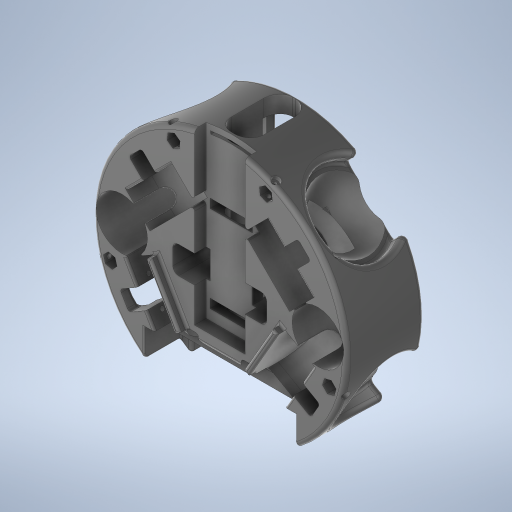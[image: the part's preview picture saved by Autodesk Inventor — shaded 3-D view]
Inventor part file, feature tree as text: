
AUTODESK INVENTOR PART (.ipt)
format: ipt  version: 2023 (Build 270158000, 158)  size: 3,521,024 bytes
history: native  units: mm
features: extrude x76, sketch x76, projected_geometry x35, fillet x19, other x16, chamfer x4, plane x2, mirror x2
ambient origin geometry x8: Origin, YZ Plane, XZ Plane, XY Plane, X Axis, Y Axis, Z Axis, Center Point
bodies: Solid1 (feature_tree)
feature tree (230):
  extrude  "Cilinder"  Depth=54.0mm TaperAngle=0.0deg
  other  "Motor Axis"
  other  "Plano M1"
  other  "Plano M2"
  other  "Plano M3"
  other  "Plano M4"
  extrude  "Roda M1"  Depth=176.0mm
  extrude  "Roda M2"  TaperAngle=60.0deg  [1 undecoded]
  extrude  "Roda M3"  TaperAngle=45.0deg  [1 undecoded]
  extrude  "Roda M4"  TaperAngle=0.0deg  [1 undecoded]
  extrude  "MotorsFitting"  Depth=14.6mm TaperAngle=0.0deg
  fillet  "MotorsCurve"  Radius=55.0mm
  extrude  "Threads M1"  Depth=20.0mm
  extrude  "Threads M2"  Depth=55.0mm
  extrude  "Threads M3"  Depth=20.0mm
  extrude  "Threads M4"  Depth=55.0mm
  extrude  "Threads Head M1"  Depth=20.0mm
  extrude  "Threads Head M2"  Depth=9.4mm
  extrude  "Threads Head M3"  Depth=9.4mm
  extrude  "Threads Head M4"  Depth=23.0mm
  extrude  "Thread Depth M1"  Depth=9.4mm
  extrude  "Thread Depth M2"  Depth=45.0mm
  extrude  "Thread Depth M3"  Depth=45.0mm
  extrude  "Thread Depth M4"  Depth=30.0mm
  extrude  "Threads Nut Head M1"  Depth=32.5mm
  extrude  "Threads Nut Head M2"  Depth=40.0mm TaperAngle=0.0deg
  extrude  "Threads Nut Head M3"  Depth=5.0mm
  extrude  "Threads Nut Head M4"  TaperAngle=0.0deg  [1 undecoded]
  extrude  "Wheel Fitting M1"  Depth=3.0mm
  extrude  "Wheel Fitting M2"  TaperAngle=0.0deg  [1 undecoded]
  extrude  "Wheel Fitting M3"  Depth=30.0mm TaperAngle=360.0deg
  extrude  "Wheel Fitting M4"  Depth=2.0mm
  extrude  "Capacitors"  Depth=6.0mm
  extrude  "Gear Entrance M1"  Depth=19.5mm
  extrude  "Gear Entrance M2"  Depth=10.0mm
  extrude  "Gear Entrance M3"  Depth=2.0mm
  extrude  "Gear Entrance M4"  Depth=3.0mm
  fillet  "Rounding Edges"  Radius=3.0mm
  fillet  "Rounding Motor Entrances"  Radius=6.0mm
  extrude  "Standoff Fitting"  TaperAngle=0.0deg  [1 undecoded]
  extrude  "Standoff Thread M1"  Depth=19.6mm
  extrude  "Standoff Thread M2"  Depth=19.5mm
  extrude  "Standoff Thread M3"  TaperAngle=0.0deg  [1 undecoded]
  extrude  "Standoff Thread M4"  Depth=30.0mm TaperAngle=360.0deg
  other  "Standoff Plane M1"
  other  "Standoff Plane M2"
  other  "Standoff Plane M3"
  other  "Standoff Plane M4"
  extrude  "Standoff Head M1"  Depth=10.0mm
  extrude  "Standoff Head M2"  Depth=2.0mm
  extrude  "Standoff Head M3"  TaperAngle=0.0deg  [1 undecoded]
  extrude  "Standoff Head M4"  Depth=6.0mm
  extrude  "Dribbler Entrance"  Depth=19.5mm
  extrude  "Battery Fitting"  Depth=3.0mm
  fillet  "Motor to Battery Edges"  Radius=3.0mm
  extrude  "Front Kicker"  Depth=11.0mm
  fillet  "Front Edges"  Radius=30.0mm
  extrude  "Cover Inlet"  Depth=10.0mm TaperAngle=0.0deg
  extrude  "Capacitors Holes"  Depth=2.0mm
  extrude  "Dribbler Motor Space"  Depth=6.0mm
  extrude  "IR Holder"  TaperAngle=0.0deg  [1 undecoded]
  fillet  "Dribbler and Kicker Edges"  Radius=19.5mm
  fillet  "Minor Fixes"  Radius=19.5mm
  chamfer  "Dribbler Chanfer"  Distance=30.0mm Angle=360.0deg
  extrude  "Capacitor Cable Fittng 1"  Depth=10.0mm TaperAngle=0.0deg
  fillet  "Capacitor Cable Rounding"  Radius=5.5mm
  extrude  "Special Nut M1"  Depth=5.5mm
  extrude  "Special Nut M2"  Depth=5.5mm
  extrude  "Special Nut M3"  Depth=5.5mm
  extrude  "Special Nut M4"  Depth=5.5mm
  extrude  "Special Nut Cylinder M1"  Depth=5.5mm
  extrude  "Special Nut Cylinder M2"  Depth=5.5mm
  extrude  "Special Nut Cylinder M3"  Depth=5.5mm
  extrude  "Special Nut Cylinder M4"  Depth=4.0mm
  fillet  "Special Nut Rounding"  Radius=4.0mm
  extrude  "Kicker Plate Fit 1"  Depth=4.0mm
  extrude  "Kicker Front Opening"  Depth=17.75mm TaperAngle=0.0deg
  extrude  "Kicker Base Fit"  Depth=4.0mm
  extrude  "Coil and Plinge Fitting"  Depth=4.0mm
  extrude  "Kicker Pkate Plunge Fit"  Depth=17.75mm TaperAngle=0.0deg
  chamfer  "Plunge Entrance 1"  Distance=17.6mm
  chamfer  "Plunge Entrance 2"  Distance=17.6mm
  fillet  "Fillet11"  Radius=15.5mm
  chamfer  "Coil Edges 1"  Distance=17.6mm
  extrude  "Kicker Plate Threads"  Depth=32.0mm
  extrude  "kicker Plate Nut 1"  Depth=35.7mm
  extrude  "Kicker Plate Nut 2"  Depth=68.0mm
  extrude  "Kicker Plunge Fit"  Depth=10.0mm TaperAngle=0.0deg
  fillet  "Kicker Plunge Round"  Radius=12.5mm
  fillet  "Wheel Round"  Radius=14.0mm
  extrude  "Capacitor Cables"  Depth=10.0mm
  fillet  "Capacitor Cable Round 1"  Radius=12.5mm
  fillet  "Capacitor Cable Round 2"  Radius=10.0mm
  extrude  "MotorProtection"  Depth=10.0mm TaperAngle=0.0deg
  fillet  "Motor Protection Round"  Radius=12.5mm
  extrude  "Extrusion86"  Depth=10.0mm
  extrude  "Extrusion87"  Depth=10.0mm TaperAngle=0.0deg
  fillet  "Fillet17"  Radius=12.5mm
  extrude  "Extrusion88"  Depth=10.0mm
  plane  "Work Plane14"
  extrude  "Extrusion89"  Depth=10.0mm TaperAngle=0.0deg
  extrude  "Extrusion91"  Depth=3.0mm
  mirror  "Mirror3"
  fillet  "Fillet18"  Radius=2.0mm
  extrude  "Extrusion92"  Depth=10.0mm
  fillet  "Fillet19"  Radius=22.0mm
  extrude  "Extrusion93"  Depth=10.0mm
  fillet  "Fillet20"  Radius=4.22mm
  extrude  "Extrusion94"  Depth=10.0mm
  extrude  "Extrusion95"  Depth=10.0mm
  other  "Eixo de trabalho1"
  other  "Eixo de trabalho2"
  other  "Eixo de trabalho3"
  other  "Eixo de trabalho4"
  other  "Plano de trabalho16"
  other  "Revolução1"
  other  "Revolução2"
  mirror  "Espelhamento5"
  sketch  "Sketch1"  dims[d0=176.0mm d1=54.0mm d2=0.0mm]
  sketch  "Sketch3"  dims[d3=180.0mm d4=176.0mm]
  sketch  "Sketch4"  dims[d5=60.0deg d6=60.0deg]
  sketch  "Sketch5"  dims[d8=45.0deg d9=45.0deg]
  sketch  "Sketch6"  dims[d10=55.0mm d11=0.0mm]
  sketch  "Sketch7"  dims[d12=20.0mm d13=14.6mm d14=0.0mm d15=55.0mm]
  sketch  "Sketch8"  dims[d16=0.0mm d17=20.0mm]
  sketch  "Sketch9"  dims[d18=14.6mm d19=0.0mm d20=55.0mm]
  sketch  "Sketch10"  dims[d21=0.0mm d22=20.0mm]
  sketch  "Sketch11"  dims[d23=14.6mm d24=0.0mm d25=55.0mm]
  sketch  "Sketch12"  dims[d26=0.0mm d27=20.0mm]
  sketch  "Sketch13"  dims[d28=14.6mm d29=0.0mm d30=9.4mm]
  sketch  "Sketch14"  dims[d32=9.4mm d33=9.4mm]
  sketch  "Sketch15"  dims[d34=23.0mm d35=23.0mm]
  sketch  "Sketch16"  dims[d37=23.0mm d38=9.4mm]
  sketch  "Sketch17"  dims[d39=23.0mm d40=45.0mm]
  sketch  "Sketch18"  dims[d41=45.0mm d42=45.0mm]
  sketch  "Sketch19"  dims[d43=45.0mm d44=30.0mm]
  sketch  "Sketch20"  dims[d45=30.0mm d46=32.5mm]
  sketch  "Sketch21"  dims[d47=32.5mm d48=40.0mm d49=0.0mm]
  sketch  "Sketch22"  dims[d50=22.5mm d51=5.0mm]
  sketch  "Sketch23"  dims[d52=12.5mm d53=0.0mm]
  sketch  "Sketch24"  dims[d54=19.5mm d55=3.0mm]
  sketch  "Sketch25"  dims[d56=19.6mm d58=0.0mm]
  sketch  "Sketch26"  dims[d59=11.0mm d60=30.0mm d62=360.0deg]
  sketch  "Sketch27"  dims[d64=2.0mm d65=2.0mm]
  sketch  "Sketch28"  dims[d66=6.0mm d67=6.0mm]
  sketch  "Sketch29"  dims[d68=19.5mm d69=19.5mm]
  sketch  "Sketch30"  dims[d70=10.0mm d71=0.0mm d72=2.5mm]
  projected_geometry  "Projected Loop1"
  sketch  "Sketch31"  dims[d73=5.0mm d74=2.0mm]
  projected_geometry  "Projected Loop2"
  sketch  "Sketch32"  dims[d75=2.0mm d76=12.5mm d77=3.0mm d78=6.0mm]
  projected_geometry  "Projected Loop3"
  sketch  "Sketch33"  dims[d79=6.0mm d80=0.0mm]
  projected_geometry  "Projected Loop4"
  sketch  "Sketch34"  dims[d81=19.5mm d82=19.6mm]
  sketch  "Sketch35"  dims[d83=19.5mm d84=19.5mm]
  projected_geometry  "Projected Loop5"
  sketch  "Sketch36"  dims[d85=5.0mm d86=0.0mm]
  projected_geometry  "Projected Loop6"
  sketch  "Sketch37"  dims[d87=11.0mm d88=30.0mm d90=360.0deg]
  projected_geometry  "Projected Loop7"
  sketch  "Sketch38"  dims[d92=10.0mm d93=0.0mm d94=5.0mm]
  projected_geometry  "Projected Loop8"
  sketch  "Sketch39"  dims[d95=12.5mm d96=2.0mm]
  sketch  "Sketch40"  dims[d97=2.0mm d98=0.0mm]
  sketch  "Sketch41"  dims[d99=19.5mm d100=6.0mm]
  sketch  "Sketch42"  dims[d101=6.0mm d102=19.5mm]
  sketch  "Sketch43"  dims[d103=19.5mm d104=19.6mm d105=3.0mm]
  sketch  "Sketch44"  dims[d106=0.0mm d107=11.0mm d108=30.0mm d110=360.0deg]
  projected_geometry  "Projected Loop9"
  projected_geometry  "Projected Loop10"
  sketch  "Sketch45"  dims[d112=5.0mm d113=10.0mm d114=0.0mm]
  sketch  "Sketch46"  dims[d115=5.0mm d116=2.0mm]
  projected_geometry  "Projected Loop11"
  projected_geometry  "Projected Loop12"
  sketch  "Sketch48"  dims[d117=2.0mm d118=6.0mm]
  projected_geometry  "Projected Loop14"
  sketch  "Sketch50"  dims[d119=6.0mm d120=0.0mm d121=19.5mm d122=19.5mm]
  projected_geometry  "Projected Loop15"
  sketch  "Sketch59"  dims[d123=19.5mm]
  sketch  "Sketch64"  dims[d124=12.5mm]
  sketch  "Sketch65"  dims[d125=19.6mm]
  projected_geometry  "Projected Loop27"
  sketch  "Sketch66"  dims[d126=3.0mm]
  projected_geometry  "Projected Loop28"
  sketch  "Sketch67"  dims[d127=0.0mm]
  sketch  "Sketch68"  dims[d128=11.0mm d129=30.0mm d131=360.0deg]
  sketch  "Sketch69"  dims[d133=2.5mm d134=10.0mm d135=0.0mm d136=5.5mm]
  sketch  "Sketch70"  dims[d137=5.5mm d138=5.5mm]
  sketch  "Sketch71"  dims[d139=18.0mm d140=0.0mm d141=5.5mm]
  sketch  "Sketch72"  dims[d142=5.5mm d143=5.5mm]
  projected_geometry  "Projected Loop29"
  sketch  "Sketch73"  dims[d144=18.0mm d145=0.0mm d146=5.5mm]
  sketch  "Sketch74"  dims[d147=5.5mm d148=5.5mm]
  projected_geometry  "Projected Loop30"
  sketch  "Sketch75"  dims[d149=18.0mm d150=0.0mm d151=5.5mm]
  projected_geometry  "Projected Loop31"
  sketch  "Sketch76"  dims[d152=5.5mm d153=5.5mm]
  projected_geometry  "Projected Loop32"
  projected_geometry  "Projected Loop33"
  sketch  "Sketch77"  dims[d154=18.0mm d155=0.0mm d156=4.0mm d157=4.0mm]
  projected_geometry  "Projected Loop34"
  projected_geometry  "Projected Loop35"
  projected_geometry  "Projected Loop36"
  projected_geometry  "Projected Loop37"
  sketch  "Sketch78"  dims[d158=17.75mm d159=0.0mm d160=4.0mm]
  sketch  "Sketch80"  dims[d161=4.0mm d162=17.75mm d163=0.0mm]
  projected_geometry  "Projected Loop38"
  projected_geometry  "Projected Loop39"
  projected_geometry  "Projected Loop40"
  projected_geometry  "Projected Loop41"
  sketch  "Sketch81"  dims[d164=4.0mm d165=4.0mm]
  sketch  "Sketch82"  dims[d166=17.75mm d167=0.0mm d168=4.0mm]
  sketch  "Sketch89"  dims[d169=4.0mm d170=17.75mm d171=0.0mm]
  sketch  "Sketch90"  dims[d172=15.5mm]
  sketch  "Sketch92"  dims[d173=32.0mm d174=17.6mm d175=0.0mm]
  sketch  "Sketch93"  dims[d176=15.5mm]
  sketch  "Sketch95"  dims[d177=32.0mm d178=17.6mm d179=0.0mm d180=15.5mm]
  plane  "Work Plane15"
  projected_geometry  "Projected Loop46"
  projected_geometry  "Projected Loop47"
  projected_geometry  "Projected Loop48"
  sketch  "Sketch97"  dims[d181=32.0mm d182=17.6mm d183=0.0mm]
  sketch  "Sketch98"  dims[d184=15.5mm d185=32.0mm]
  projected_geometry  "Projected Loop49"
  projected_geometry  "Projected Loop50"
  projected_geometry  "Projected Loop51"
  sketch  "Sketch99"  dims[d186=17.6mm d187=0.0mm d188=35.7mm]
  sketch  "Esboço100"  dims[d189=4.15mm d190=68.0mm]
  sketch  "Esboço101"  dims[d191=68.0mm d192=50.0mm d193=0.0mm d195=12.5mm d196=14.0mm d197=0.0mm d198=10.0mm d199=12.5mm d200=10.0mm d201=14.0mm d202=0.0mm d203=12.5mm d204=10.0mm d205=14.0mm d206=0.0mm d207=12.5mm d208=10.0mm d209=14.0mm d210=0.0mm d211=3.0mm d212=2.0mm d213=2.0mm d214=2.0mm d215=22.0mm d216=76.0mm d217=4.22mm d218=72.0mm d219=32.0mm d220=4.22mm d221=8.0mm d222=0.0mm d223=3.0mm d224=3.5mm d225=2.436418mm d226=24.0mm d227=0.0mm d228=3.0mm d229=3.5mm d230=2.436418mm d231=24.0mm d232=0.0mm d233=3.0mm d234=3.5mm d235=2.436418mm d236=24.0mm d237=0.0mm d238=3.0mm d239=3.5mm d240=2.436418mm d241=24.0mm d242=0.0mm d243=90.0mm d244=40.0mm d245=0.0mm d246=55.0mm d247=10.0mm d248=0.0mm d249=2.0mm d250=0.0mm d251=2.0mm d252=0.0mm d253=2.0mm d254=0.0mm d255=2.0mm d256=0.0mm d257=2.0mm d258=1.5mm d259=35.0mm d260=120.0mm d261=0.0mm d262=28.5mm d263=8.0mm d264=0.0mm d265=1.5mm d266=-2.0mm d267=-2.0mm d268=-2.0mm d269=-2.0mm d270=5.5mm d271=4.0mm d272=0.0mm d273=5.5mm d274=4.0mm d275=0.0mm d276=5.5mm d277=4.0mm d278=0.0mm d279=5.5mm d280=4.0mm d281=0.0mm d282=56.5mm d283=12.5mm d284=0.0mm d285=17.0mm d286=10.0mm d287=0.0mm d288=2.0mm d289=3.0mm d299=82.0mm d300=17.453293mm d301=3.490659mm d302=84.0mm d303=17.453293mm d304=3.490659mm d305=8.0mm d306=0.0mm d307=0.4mm d308=22.0mm d309=22.0mm d310=10.0mm d311=0.0mm d317=90.0mm d318=14.0mm d319=0.0mm d320=0.0mm d321=11.0mm d322=0.0mm d327=3.75mm d328=17.11mm d329=0.0mm d330=24.43461mm d331=7.1mm d332=0.0mm d355=2.0mm d356=2.0mm d357=45.0deg d358=3.0mm d359=2.0mm d396=5.5mm d397=10.0mm d398=23.0mm d399=16.0mm d400=56.0mm d401=0.0mm d402=5.5mm d403=0.0mm d404=1.5mm d429=8.1mm d430=16.1mm d431=6.0mm d432=3.0mm d433=0.0mm d434=0.0mm d435=16.1mm d436=8.1mm d437=6.0mm d438=3.0mm d439=0.0mm d440=0.0mm d441=16.1mm d442=8.1mm d443=6.0mm d444=3.0mm d445=0.0mm d446=0.0mm d447=8.1mm d448=16.1mm d449=6.0mm d450=3.0mm d451=0.0mm d452=0.0mm d453=8.1mm d454=5.75mm d455=0.0mm d456=8.1mm d457=5.75mm d458=0.0mm d459=8.1mm d460=5.75mm d461=0.0mm d462=8.1mm d463=5.75mm d464=0.0mm d465=0.9mm d466=29.2mm d467=135.0mm d468=0.0mm d469=14.6mm d470=76.25mm d471=43.2mm d472=7.1mm d473=0.0mm d474=43.2mm d475=7.1mm d476=0.0mm d477=34.5mm d478=79.5mm d479=6.0mm d480=0.0mm d481=30.9mm d482=41.0mm d483=0.0mm d485=29.2mm d486=6.2mm d490=46.1mm d491=0.0mm d492=29.2mm d493=6.2mm d494=3.6mm d495=3.6mm d496=44.8mm d497=0.0mm d498=7.0mm d499=0.0mm d500=6.4mm d501=3.6mm d502=45.0deg d503=6.4mm d504=3.6mm d505=45.0deg d507=10.0mm d508=7.5mm d509=4.6mm d510=60.0deg d511=3.0mm d512=3.0mm d513=18.0mm d514=18.0mm d515=3.0mm d516=3.0mm d517=18.0mm d518=18.0mm d519=3.55mm d520=3.55mm d521=3.55mm d522=3.55mm d523=12.0mm d524=0.0mm d525=5.6mm d526=2.4mm d527=5.6mm d528=2.4mm d529=3.0mm d530=3.0mm d531=1.3mm d532=1.3mm d533=39.8mm d534=0.0mm d535=60.0deg d536=60.0deg d537=120.0deg d538=120.0deg d539=60.0deg d540=60.0deg d541=120.0deg d542=120.0deg d543=10.0mm d544=0.0mm d545=22.0mm d546=20.0mm d547=11.0mm d548=12.5mm d549=10.0mm d550=0.0mm d551=10.0mm d552=3.0mm d553=2.0mm d554=3.0mm d555=18.0mm d556=19.0mm d557=18.0mm d558=19.0mm d559=23.6mm d560=23.6mm d561=7.5mm d562=7.5mm d563=47.0mm d564=0.0mm d565=2.0mm d566=2.0mm d567=4.0mm d568=5.0mm d609=0.0mm d611=5.0mm d612=0.0mm d613=3.75mm d614=0.0mm d616=0.0mm d617=5.0mm d618=3.75mm d619=6.0mm d620=0.0mm d621=1.75mm d622=0.75mm d623=5.5mm d624=9.5mm d625=9.25mm d626=25.9mm d627=8.5mm d628=0.0mm d632=3.0mm d633=0.0mm d636=7.4mm d637=0.0mm d638=3.0mm d639=3.0mm d640=4.0mm d641=3.75mm d642=131.25mm d643=0.0mm d644=-8.0mm d645=5.5mm d646=10.0mm d647=0.0mm d650=10.0mm d651=10.0mm d653=16.0mm d654=2.5mm d655=0.0mm d656=1.0mm d657=2.0mm d664=1.0mm d665=0.0mm d666=19.9mm d667=0.5mm d668=53.9mm d669=25.0mm d670=10.25mm d671=26.12407mm d672=8.0mm d673=90.0deg d674=90.0deg d675=90.0deg d676=90.0deg d677=90.0deg d678=90.0deg d679=90.0deg d680=4.0mm d681=2.0mm d682=29.2mm d683=10.0mm d684=0.0mm d685=2.0mm d686=0.5mm d687=3.0mm d688=3.0mm d689=6.5mm d691=6.5mm d692=4.0mm d693=10.0mm d694=0.0mm d695=5.5mm d696=5.5mm d697=2.0mm d698=2.1mm d699=0.0mm d700=0.0mm d701=4.0mm d702=0.0mm d703=50.0mm d704=82.5mm d705=90.0deg d706=50.0mm d707=82.5mm d708=90.0deg]
note: 9 required parameter values undecoded (feature->parameter linkage not recoverable at this tier; creation-order binding heuristic only, values carry confidence <= 0.55)
